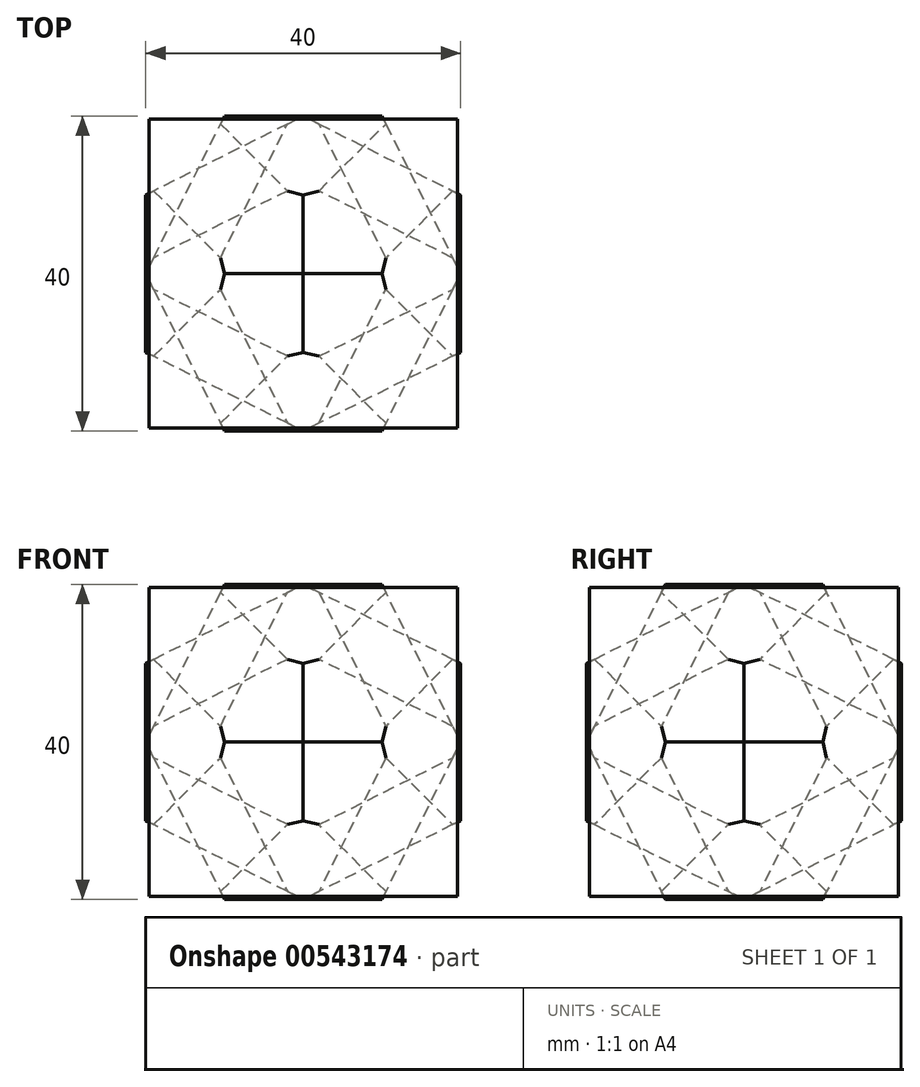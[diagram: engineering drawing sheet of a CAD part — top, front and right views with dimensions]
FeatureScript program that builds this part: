
annotation { "Feature Type Name" : "Feature", "Feature Type Description" : "" }
export const myFeature = defineFeature(function(context is Context, id is Id, definition is map)
    precondition{}
    {
        {
            var Q0;
            Q0=qCreatedBy(makeId("Front.planeOp"),FACE);
            var sketch = newSketch(context, id + "F0", { "sketchPlane" : qUnion([Q0])});
            skLineSegment(sketch, "E0", {"start": v(40, 0) * mm, "end": v(0, 20) * mm});
            skLineSegment(sketch, "E1", {"start": v(0, 20) * mm, "end": v(-40, 0) * mm});
            skLineSegment(sketch, "E2", {"start": v(-40, 0) * mm, "end": v(0, -20) * mm});
            skLineSegment(sketch, "E3", {"start": v(0, -20) * mm, "end": v(40, 0) * mm});
            skSolve(sketch);
        }
        {
            var Q0;
            Q0=makeQuery(id+"F0.imprint","IMPRINT",FACE,{"disambiguationData":[TD([[makeQuery(id+"F0.imprint","IMPRINT",EDGE,{"derivedFrom":sQuery(id+"F0.wireOp",EDGE,"E0")}),1.0]])]});
            extrude(context, id + "F1", {"entities" : qUnion([Q0]), "depth" : 25 * mm, "offsetDistance" : 25 * mm, "hasSecondDirection" : true, "secondDirectionOppositeDirection" : true, "secondDirectionDepth" : 25 * mm});
        }
        {
            var Q0;
            Q0=qCreatedBy(makeId("Front.planeOp"),FACE);
            var sketch = newSketch(context, id + "F2", { "sketchPlane" : qUnion([Q0])});
            skLineSegment(sketch, "E4", {"start": v(0, 49.78) * mm, "end": v(0, 0) * mm});
            skSolve(sketch);
        }
        {
            var Q0;
            Q0=qCreatedBy(makeId("Front.planeOp"),FACE);
            var sketch = newSketch(context, id + "F3", { "sketchPlane" : qUnion([Q0])});
            skLineSegment(sketch, "E5", {"start": v(60.84, 0) * mm, "end": v(0, 0) * mm});
            skSolve(sketch);
        }
        {
            var Q0;
            Q0=qCreatedBy(makeId("Right.planeOp"),FACE);
            var sketch = newSketch(context, id + "F4", { "sketchPlane" : qUnion([Q0])});
            skLineSegment(sketch, "E6", {"start": v(48.72, 0) * mm, "end": v(-1.84, 0) * mm});
            skSolve(sketch);
        }
        {
            var Q0;
            Q0=makeQuery(id+"F1.opExtrude","SWEPT_BODY",BODY,{"disambiguationData":[OSD([sQuery(id+"F0.wireOp",EDGE,"E0"),sQuery(id+"F0.wireOp",EDGE,"E1"),sQuery(id+"F0.wireOp",EDGE,"E2"),sQuery(id+"F0.wireOp",EDGE,"E3")])]});
            var Q1;
            Q1=sQuery(id+"F2.wireOp",EDGE,"E4");
            transform(context, id + "F5", {"entities" : qUnion([Q0]), "transformType" : TransformType.ROTATION, "transformAxis" : qUnion([Q1]), "angle" : 90 * degree, "makeCopy" : true});
        }
        {
            var Q0;
            Q0=makeQuery(id+"F5.opPattern","COPY",BODY,{"derivedFrom":makeQuery(id+"F1.opExtrude","SWEPT_BODY",BODY,{"disambiguationData":[OSD([sQuery(id+"F0.wireOp",EDGE,"E0"),sQuery(id+"F0.wireOp",EDGE,"E1"),sQuery(id+"F0.wireOp",EDGE,"E2"),sQuery(id+"F0.wireOp",EDGE,"E3")])]}),"instanceName":"1"});
            var Q1;
            Q1=sQuery(id+"F4.wireOp",EDGE,"E6");
            transform(context, id + "F6", {"entities" : qUnion([Q0]), "transformType" : TransformType.ROTATION, "transformAxis" : qUnion([Q1]), "angle" : 90 * degree, "makeCopy" : true});
        }
        {
            var Q0;
            Q0=makeQuery(id+"F5.opPattern","COPY",BODY,{"derivedFrom":makeQuery(id+"F1.opExtrude","SWEPT_BODY",BODY,{"disambiguationData":[OSD([sQuery(id+"F0.wireOp",EDGE,"E0"),sQuery(id+"F0.wireOp",EDGE,"E1"),sQuery(id+"F0.wireOp",EDGE,"E2"),sQuery(id+"F0.wireOp",EDGE,"E3")])]}),"instanceName":"1"});
            var Q1;
            Q1=sQuery(id+"F3.wireOp",EDGE,"E5");
            transform(context, id + "F7", {"entities" : qUnion([Q0]), "transformType" : TransformType.ROTATION, "transformAxis" : qUnion([Q1]), "angle" : 90 * degree, "makeCopy" : false});
        }
        {
            var Q0;
            Q0=makeQuery(id+"F5.opPattern","COPY",BODY,{"derivedFrom":makeQuery(id+"F1.opExtrude","SWEPT_BODY",BODY,{"disambiguationData":[OSD([sQuery(id+"F0.wireOp",EDGE,"E0"),sQuery(id+"F0.wireOp",EDGE,"E1"),sQuery(id+"F0.wireOp",EDGE,"E2"),sQuery(id+"F0.wireOp",EDGE,"E3")])]}),"instanceName":"1"});
            var Q1;
            Q1=makeQuery(id+"F6.opPattern","COPY",BODY,{"derivedFrom":makeQuery(id+"F5.opPattern","COPY",BODY,{"derivedFrom":makeQuery(id+"F1.opExtrude","SWEPT_BODY",BODY,{"disambiguationData":[OSD([sQuery(id+"F0.wireOp",EDGE,"E0"),sQuery(id+"F0.wireOp",EDGE,"E1"),sQuery(id+"F0.wireOp",EDGE,"E2"),sQuery(id+"F0.wireOp",EDGE,"E3")])]}),"instanceName":"1"}),"instanceName":"1"});
            booleanBodies(context, id + "F8", {"operationType" : BooleanOperationType.INTERSECTION, "tools" : qUnion([Q0, Q1])});
        }
        {
            var Q0;
            {var subQ0=makeQuery(id+"F5.opPattern","COPY",BODY,{"derivedFrom":makeQuery(id+"F1.opExtrude","SWEPT_BODY",BODY,{"disambiguationData":[OSD([sQuery(id+"F0.wireOp",EDGE,"E0"),sQuery(id+"F0.wireOp",EDGE,"E1"),sQuery(id+"F0.wireOp",EDGE,"E2"),sQuery(id+"F0.wireOp",EDGE,"E3")])]}),"instanceName":"1"});Q0=makeQuery(id+"F8.opBoolean","INTERSECT",BODY,{"derivedFrom":[subQ0,makeQuery(id+"F6.opPattern","COPY",BODY,{"derivedFrom":subQ0,"instanceName":"1"})]});}
            var Q1;
            Q1=makeQuery(id+"F1.opExtrude","SWEPT_BODY",BODY,{"disambiguationData":[OSD([sQuery(id+"F0.wireOp",EDGE,"E0"),sQuery(id+"F0.wireOp",EDGE,"E1"),sQuery(id+"F0.wireOp",EDGE,"E2"),sQuery(id+"F0.wireOp",EDGE,"E3")])]});
            booleanBodies(context, id + "F9", {"operationType" : BooleanOperationType.INTERSECTION, "tools" : qUnion([Q0, Q1])});
        }
        {
            var Q0;
            Q0=qCreatedBy(makeId("Top.planeOp"),FACE);
            var sketch = newSketch(context, id + "F10", { "sketchPlane" : qUnion([Q0])});
            skLineSegment(sketch, "E7", {"start": v(20, 0) * mm, "end": v(0, 20) * mm});
            skLineSegment(sketch, "E8", {"start": v(0, 20) * mm, "end": v(-20, 0) * mm});
            skLineSegment(sketch, "E9", {"start": v(-20, 0) * mm, "end": v(0, -20) * mm});
            skLineSegment(sketch, "E10", {"start": v(0, -20) * mm, "end": v(20, 0) * mm});
            skSolve(sketch);
        }
        {
            var Q0;
            Q0=qSketchRegion(id+"F10",true);
            extrude(context, id + "F11", {"entities" : qUnion([Q0]), "depth" : 20 * mm, "offsetDistance" : 25 * mm, "hasDraft" : true, "draftAngle" : atan(1 / sqrt(2)), "draftPullDirection" : true, "hasSecondDirection" : true, "secondDirectionOppositeDirection" : true, "secondDirectionDepth" : 20 * mm, "hasSecondDirectionDraft" : true, "secondDirectionDraftAngle" : atan(1 / sqrt(2)), "secondDirectionDraftPullDirection" : true});
        }
        {
            var Q0;
            {var subQ0=makeQuery(id+"F1.opExtrude","SWEPT_BODY",BODY,{"disambiguationData":[OSD([sQuery(id+"F0.wireOp",EDGE,"E0"),sQuery(id+"F0.wireOp",EDGE,"E1"),sQuery(id+"F0.wireOp",EDGE,"E2"),sQuery(id+"F0.wireOp",EDGE,"E3")])]});var subQ1=makeQuery(id+"F5.opPattern","COPY",BODY,{"derivedFrom":subQ0,"instanceName":"1"});Q0=makeQuery(id+"F9.opBoolean","INTERSECT",BODY,{"derivedFrom":[subQ0,makeQuery(id+"F8.opBoolean","INTERSECT",BODY,{"derivedFrom":[subQ1,makeQuery(id+"F6.opPattern","COPY",BODY,{"derivedFrom":subQ1,"instanceName":"1"})]})]});}
            transform(context, id + "F12", {"entities" : qUnion([Q0]), "transformType" : TransformType.TRANSLATION_3D, "dx" : 50 * mm, "dy" : 0 * mm, "dz" : 0 * mm, "makeCopy" : false});
        }
        {
            var Q0;
            Q0=makeQuery(id+"F11.*.split.splitOp","SPLIT",BODY,{"derivedFrom":makeQuery(id+"F11.opExtrude","SWEPT_BODY",BODY,{"disambiguationData":[OSD([sQuery(id+"F10.wireOp",EDGE,"E7"),sQuery(id+"F10.wireOp",EDGE,"E8"),sQuery(id+"F10.wireOp",EDGE,"E9"),sQuery(id+"F10.wireOp",EDGE,"E10")])]})});
            var Q1;
            Q1=qCreatedBy(makeId("Origin.pointOp"),VERTEX);
            transform(context, id + "F13", {"entities" : qUnion([Q0]), "transformType" : TransformType.SCALE_UNIFORMLY, "scale" : 1.5, "scalePoint" : qUnion([Q1]), "makeCopy" : false});
        }
        {
            var Q0;
            {var subQ0=makeQuery(id+"F1.opExtrude","SWEPT_BODY",BODY,{"disambiguationData":[OSD([sQuery(id+"F0.wireOp",EDGE,"E0"),sQuery(id+"F0.wireOp",EDGE,"E1"),sQuery(id+"F0.wireOp",EDGE,"E2"),sQuery(id+"F0.wireOp",EDGE,"E3")])]});var subQ1=makeQuery(id+"F5.opPattern","COPY",BODY,{"derivedFrom":subQ0,"instanceName":"1"});Q0=makeQuery(id+"F9.opBoolean","INTERSECT",BODY,{"derivedFrom":[subQ0,makeQuery(id+"F8.opBoolean","INTERSECT",BODY,{"derivedFrom":[subQ1,makeQuery(id+"F6.opPattern","COPY",BODY,{"derivedFrom":subQ1,"instanceName":"1"})]})]});}
            transform(context, id + "F14", {"entities" : qUnion([Q0]), "transformType" : TransformType.TRANSLATION_3D, "dx" : -50 * mm, "dy" : 0 * mm, "dz" : 0 * mm, "makeCopy" : false});
        }
        {
            var Q0;
            Q0=makeQuery(id+"F11.*.split.splitOp","SPLIT",BODY,{"derivedFrom":makeQuery(id+"F11.opExtrude","SWEPT_BODY",BODY,{"disambiguationData":[OSD([sQuery(id+"F10.wireOp",EDGE,"E7"),sQuery(id+"F10.wireOp",EDGE,"E8"),sQuery(id+"F10.wireOp",EDGE,"E9"),sQuery(id+"F10.wireOp",EDGE,"E10")])]})});
            var Q1;
            Q1=qCreatedBy(makeId("Origin.pointOp"),VERTEX);
            transform(context, id + "F15", {"entities" : qUnion([Q0]), "transformType" : TransformType.SCALE_UNIFORMLY, "scale" : 1.05, "scalePoint" : qUnion([Q1]), "makeCopy" : false});
        }
        {
            var Q0;
            Q0=makeQuery(id+"F11.*.split.splitOp","SPLIT",BODY,{"derivedFrom":makeQuery(id+"F11.opExtrude","SWEPT_BODY",BODY,{"disambiguationData":[OSD([sQuery(id+"F10.wireOp",EDGE,"E7"),sQuery(id+"F10.wireOp",EDGE,"E8"),sQuery(id+"F10.wireOp",EDGE,"E9"),sQuery(id+"F10.wireOp",EDGE,"E10")])]})});
            var Q1;
            {var subQ0=makeQuery(id+"F1.opExtrude","SWEPT_BODY",BODY,{"disambiguationData":[OSD([sQuery(id+"F0.wireOp",EDGE,"E0"),sQuery(id+"F0.wireOp",EDGE,"E1"),sQuery(id+"F0.wireOp",EDGE,"E2"),sQuery(id+"F0.wireOp",EDGE,"E3")])]});var subQ1=makeQuery(id+"F5.opPattern","COPY",BODY,{"derivedFrom":subQ0,"instanceName":"1"});Q1=makeQuery(id+"F9.opBoolean","INTERSECT",BODY,{"derivedFrom":[subQ0,makeQuery(id+"F8.opBoolean","INTERSECT",BODY,{"derivedFrom":[subQ1,makeQuery(id+"F6.opPattern","COPY",BODY,{"derivedFrom":subQ1,"instanceName":"1"})]})]});}
            booleanBodies(context, id + "F16", {"operationType" : BooleanOperationType.INTERSECTION, "tools" : qUnion([Q0, Q1])});
        }
        {
            var Q0;
            {var subQ0=makeQuery(id+"F1.opExtrude","SWEPT_BODY",BODY,{"disambiguationData":[OSD([sQuery(id+"F0.wireOp",EDGE,"E0"),sQuery(id+"F0.wireOp",EDGE,"E1"),sQuery(id+"F0.wireOp",EDGE,"E2"),sQuery(id+"F0.wireOp",EDGE,"E3")])]});var subQ1=makeQuery(id+"F5.opPattern","COPY",BODY,{"derivedFrom":subQ0,"instanceName":"1"});Q0=makeQuery(id+"F16.opBoolean","INTERSECT",BODY,{"derivedFrom":[makeQuery(id+"F9.opBoolean","INTERSECT",BODY,{"derivedFrom":[subQ0,makeQuery(id+"F8.opBoolean","INTERSECT",BODY,{"derivedFrom":[subQ1,makeQuery(id+"F6.opPattern","COPY",BODY,{"derivedFrom":subQ1,"instanceName":"1"})]})]}),makeQuery(id+"F11.*.split.splitOp","SPLIT",BODY,{"derivedFrom":makeQuery(id+"F11.opExtrude","SWEPT_BODY",BODY,{"disambiguationData":[OSD([sQuery(id+"F10.wireOp",EDGE,"E7"),sQuery(id+"F10.wireOp",EDGE,"E8"),sQuery(id+"F10.wireOp",EDGE,"E9"),sQuery(id+"F10.wireOp",EDGE,"E10")])]})})]});}
            var Q1;
            Q1=sQuery(id+"F2.wireOp",EDGE,"E4");
            transform(context, id + "F17", {"entities" : qUnion([Q0]), "transformType" : TransformType.ROTATION, "transformAxis" : qUnion([Q1]), "angle" : 90 * degree, "makeCopy" : true});
        }
        {
            var Q0;
            Q0=qCreatedBy(makeId("Top.planeOp"),FACE);
            var sketch = newSketch(context, id + "F18", { "sketchPlane" : qUnion([Q0])});
            skLineSegment(sketch, "E11", {"start": v(-20, -20) * mm, "end": v(20, -20) * mm});
            skLineSegment(sketch, "E12", {"start": v(20, -20) * mm, "end": v(20, 20) * mm});
            skLineSegment(sketch, "E13", {"start": v(20, 20) * mm, "end": v(-20, 20) * mm});
            skLineSegment(sketch, "E14", {"start": v(-20, 20) * mm, "end": v(-20, -20) * mm});
            skSolve(sketch);
        }
        {
            var Q0;
            Q0=makeQuery(id+"F18.imprint","IMPRINT",FACE,{"disambiguationData":[TD([[makeQuery(id+"F18.imprint","IMPRINT",EDGE,{"derivedFrom":sQuery(id+"F18.wireOp",EDGE,"E11")}),1.0]])]});
            extrude(context, id + "F19", {"entities" : qUnion([Q0]), "depth" : 20 * mm, "offsetDistance" : 25 * mm, "hasSecondDirection" : true, "secondDirectionOppositeDirection" : true, "secondDirectionDepth" : 20 * mm});
        }
        {
            var Q0;
            Q0=makeQuery(id+"F19.opExtrude","SWEPT_BODY",BODY,{"disambiguationData":[OSD([sQuery(id+"F18.wireOp",EDGE,"E11"),sQuery(id+"F18.wireOp",EDGE,"E12"),sQuery(id+"F18.wireOp",EDGE,"E13"),sQuery(id+"F18.wireOp",EDGE,"E14")])]});
            var Q1;
            Q1=sQuery(id+"F2.wireOp",VERTEX,"E4.end");
            transform(context, id + "F20", {"entities" : qUnion([Q0]), "transformType" : TransformType.SCALE_UNIFORMLY, "scale" : 0.98, "scalePoint" : qUnion([Q1]), "makeCopy" : false});
        }
    });
